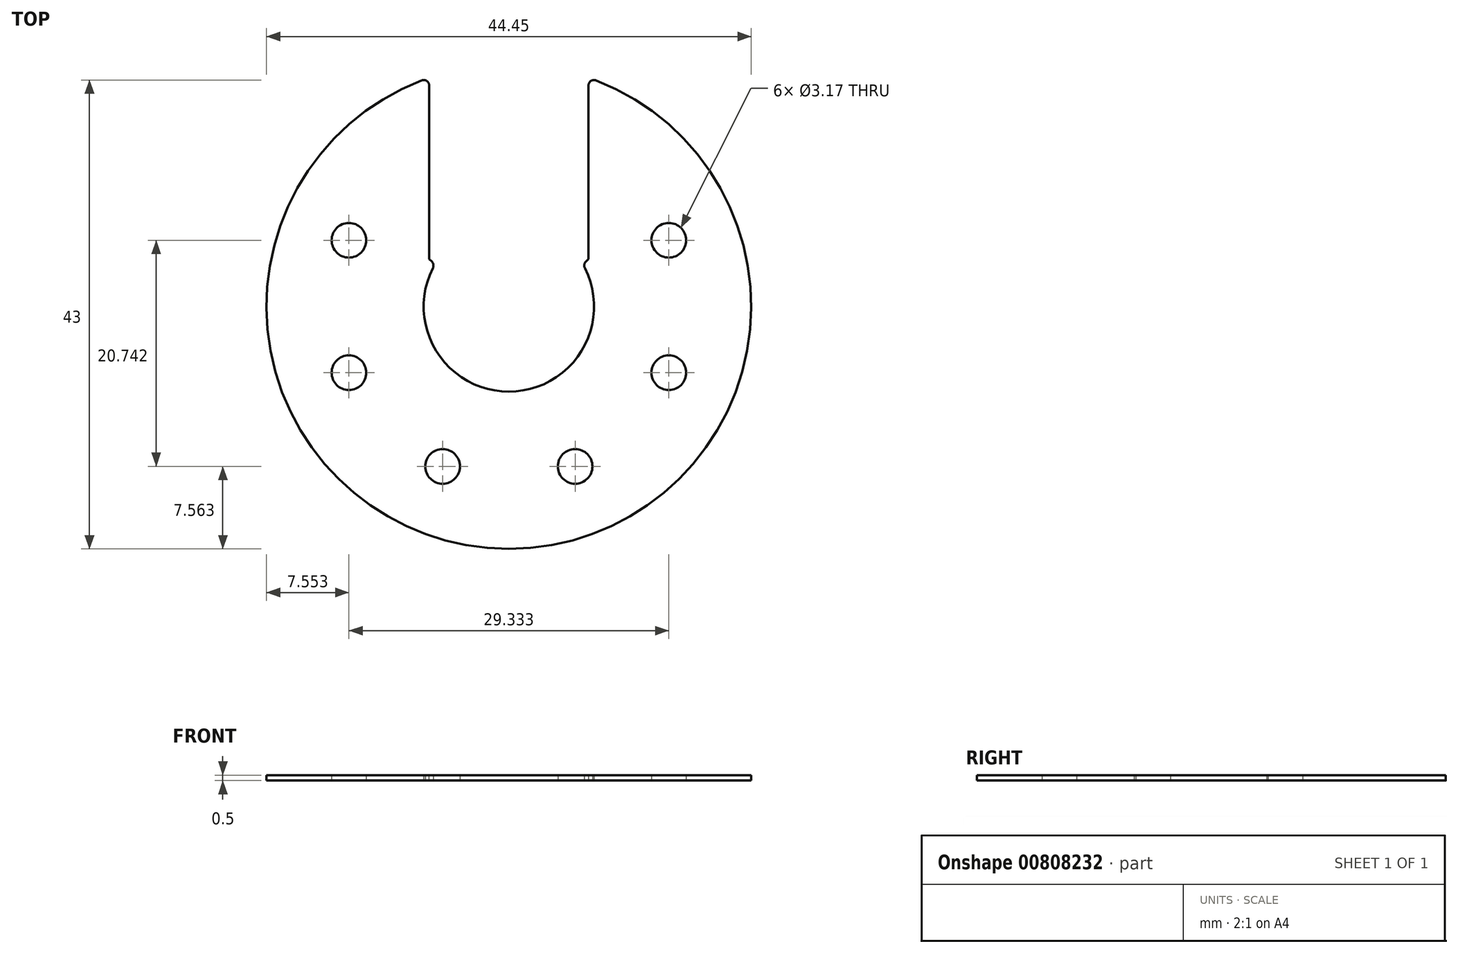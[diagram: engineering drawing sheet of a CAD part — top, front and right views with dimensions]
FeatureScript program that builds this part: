
annotation { "Feature Type Name" : "Feature", "Feature Type Description" : "" }
export const myFeature = defineFeature(function(context is Context, id is Id, definition is map)
    precondition{}
    {
        {
            assignVariable(context, id + "F0", {"name" : "h", "anyValue" : 0.5});
        }
        {
            var Q0;
            Q0=qCreatedBy(makeId("Top.planeOp"),FACE);
            var sketch = newSketch(context, id + "F1", { "sketchPlane" : qUnion([Q0])});
            skArc(sketch, "E0", {"start": v(-7.3, 21) * mm, "mid": v(0, -22.23) * mm, "end": v(7.3, 21) * mm});
            skArc(sketch, "E1", {"start": v(-6.8, 3.85) * mm, "mid": v(0, -7.81) * mm, "end": v(6.8, 3.85) * mm});
            skLineSegment(sketch, "E2", {"start": v(-7.3, 21) * mm, "end": v(-7.3, 4.35) * mm});
            skLineSegment(sketch, "E3.MirrorCS", {"start": v(7.3, 21) * mm, "end": v(7.3, 4.35) * mm});
            skLineSegment(sketch, "E4", {"start": v(-6.8, 3.85) * mm, "end": v(-7.3, 4.35) * mm});
            skLineSegment(sketch, "E5.MirrorCS", {"start": v(6.8, 3.85) * mm, "end": v(7.3, 4.35) * mm});
            skPoint(sketch, "E6.orphan", {"position": v(7.3, 2.77) * mm});
            skPoint(sketch, "E7.orphan", {"position": v(-7.3, 2.77) * mm});
            skSolve(sketch);
        }
        {
            var Q0;
            Q0=qCreatedBy(makeId("Top.planeOp"),FACE);
            var sketch = newSketch(context, id + "F2", { "sketchPlane" : qUnion([Q0])});
            skCircle(sketch, "E8", {"center": v(0, 0) * mm, "radius": 15.88 * mm, "construction": true});
            skCircle(sketch, "E9", {"center": v(-14.67, 6.08) * mm, "radius": 1.59 * mm});
            skLineSegment(sketch, "E10", {"start": v(-14.67, 6.08) * mm, "end": v(0, 0) * mm, "construction": true});
            skCircle(sketch, "E11.1.0", {"center": v(-14.67, -6.08) * mm, "radius": 1.59 * mm});
            skCircle(sketch, "E11.2.0", {"center": v(-6.08, -14.67) * mm, "radius": 1.59 * mm});
            skCircle(sketch, "E11.3.0", {"center": v(6.08, -14.67) * mm, "radius": 1.59 * mm});
            skCircle(sketch, "E11.4.0", {"center": v(14.67, -6.08) * mm, "radius": 1.59 * mm});
            skCircle(sketch, "E11.5.0", {"center": v(14.67, 6.08) * mm, "radius": 1.59 * mm});
            skLineSegment(sketch, "E11.anchor1", {"start": v(0, 0) * mm, "end": v(-14.67, 6.08) * mm, "construction": true});
            skLineSegment(sketch, "E11.anchor2", {"start": v(0, 0) * mm, "end": v(14.67, 6.08) * mm, "construction": true});
            skSolve(sketch);
        }
        {
            var Q0;
            Q0=makeQuery(id+"F1.imprint","IMPRINT",FACE,{"disambiguationData":[TD([[makeQuery(id+"F1.imprint","IMPRINT",EDGE,{"derivedFrom":sQuery(id+"F1.wireOp",EDGE,"E0")}),1.0]])]});
            extrude(context, id + "F3", {"entities" : qUnion([Q0]), "depth" : (getVariable(context, 'h')) * mm, "offsetDistance" : 25.4 * mm});
        }
        {
            var Q0;
            Q0=makeQuery(id+"F3.opExtrude","SWEPT_EDGE",EDGE,{"disambiguationData":[OSD([sQuery(id+"F1.wireOp",EDGE,"E1"),sQuery(id+"F1.wireOp",EDGE,"E4")])]});
            var Q1;
            Q1=makeQuery(id+"F3.opExtrude","SWEPT_EDGE",EDGE,{"disambiguationData":[OSD([sQuery(id+"F1.wireOp",EDGE,"E1"),sQuery(id+"F1.wireOp",EDGE,"E5.MirrorCS")])]});
            var Q2;
            Q2=makeQuery(id+"F3.opExtrude","SWEPT_EDGE",EDGE,{"disambiguationData":[OSD([sQuery(id+"F1.wireOp",EDGE,"E0"),sQuery(id+"F1.wireOp",EDGE,"E2")])]});
            var Q3;
            Q3=makeQuery(id+"F3.opExtrude","SWEPT_EDGE",EDGE,{"disambiguationData":[OSD([sQuery(id+"F1.wireOp",EDGE,"E0"),sQuery(id+"F1.wireOp",EDGE,"E3.MirrorCS")])]});
            fillet(context, id + "F4", {"entities" : qUnion([Q0, Q1, Q2, Q3]), "radius" : 0.5 * mm, "tangentPropagation" : true, "allowEdgeOverflow" : false});
        }
        {
            var Q0;
            Q0=makeQuery(id+"F2.imprint","IMPRINT",FACE,{"disambiguationData":[TD([[makeQuery(id+"F2.imprint","IMPRINT",EDGE,{"derivedFrom":sQuery(id+"F2.wireOp",EDGE,"E9")}),1.0]])]});
            var Q1;
            Q1=makeQuery(id+"F2.imprint","IMPRINT",FACE,{"disambiguationData":[TD([[makeQuery(id+"F2.imprint","IMPRINT",EDGE,{"derivedFrom":sQuery(id+"F2.wireOp",EDGE,"E11.1.0")}),1.0]])]});
            var Q2;
            Q2=makeQuery(id+"F2.imprint","IMPRINT",FACE,{"disambiguationData":[TD([[makeQuery(id+"F2.imprint","IMPRINT",EDGE,{"derivedFrom":sQuery(id+"F2.wireOp",EDGE,"E11.2.0")}),1.0]])]});
            var Q3;
            Q3=makeQuery(id+"F2.imprint","IMPRINT",FACE,{"disambiguationData":[TD([[makeQuery(id+"F2.imprint","IMPRINT",EDGE,{"derivedFrom":sQuery(id+"F2.wireOp",EDGE,"E11.3.0")}),1.0]])]});
            var Q4;
            Q4=makeQuery(id+"F2.imprint","IMPRINT",FACE,{"disambiguationData":[TD([[makeQuery(id+"F2.imprint","IMPRINT",EDGE,{"derivedFrom":sQuery(id+"F2.wireOp",EDGE,"E11.4.0")}),1.0]])]});
            var Q5;
            Q5=makeQuery(id+"F2.imprint","IMPRINT",FACE,{"disambiguationData":[TD([[makeQuery(id+"F2.imprint","IMPRINT",EDGE,{"derivedFrom":sQuery(id+"F2.wireOp",EDGE,"E11.5.0")}),1.0]])]});
            extrude(context, id + "F5", {"entities" : qUnion([Q0, Q1, Q2, Q3, Q4, Q5]), "operationType" : NewBodyOperationType.REMOVE, "endBound" : BoundingType.UP_TO_NEXT, "depth" : 25.4 * mm, "offsetDistance" : 25.4 * mm});
        }
    });
